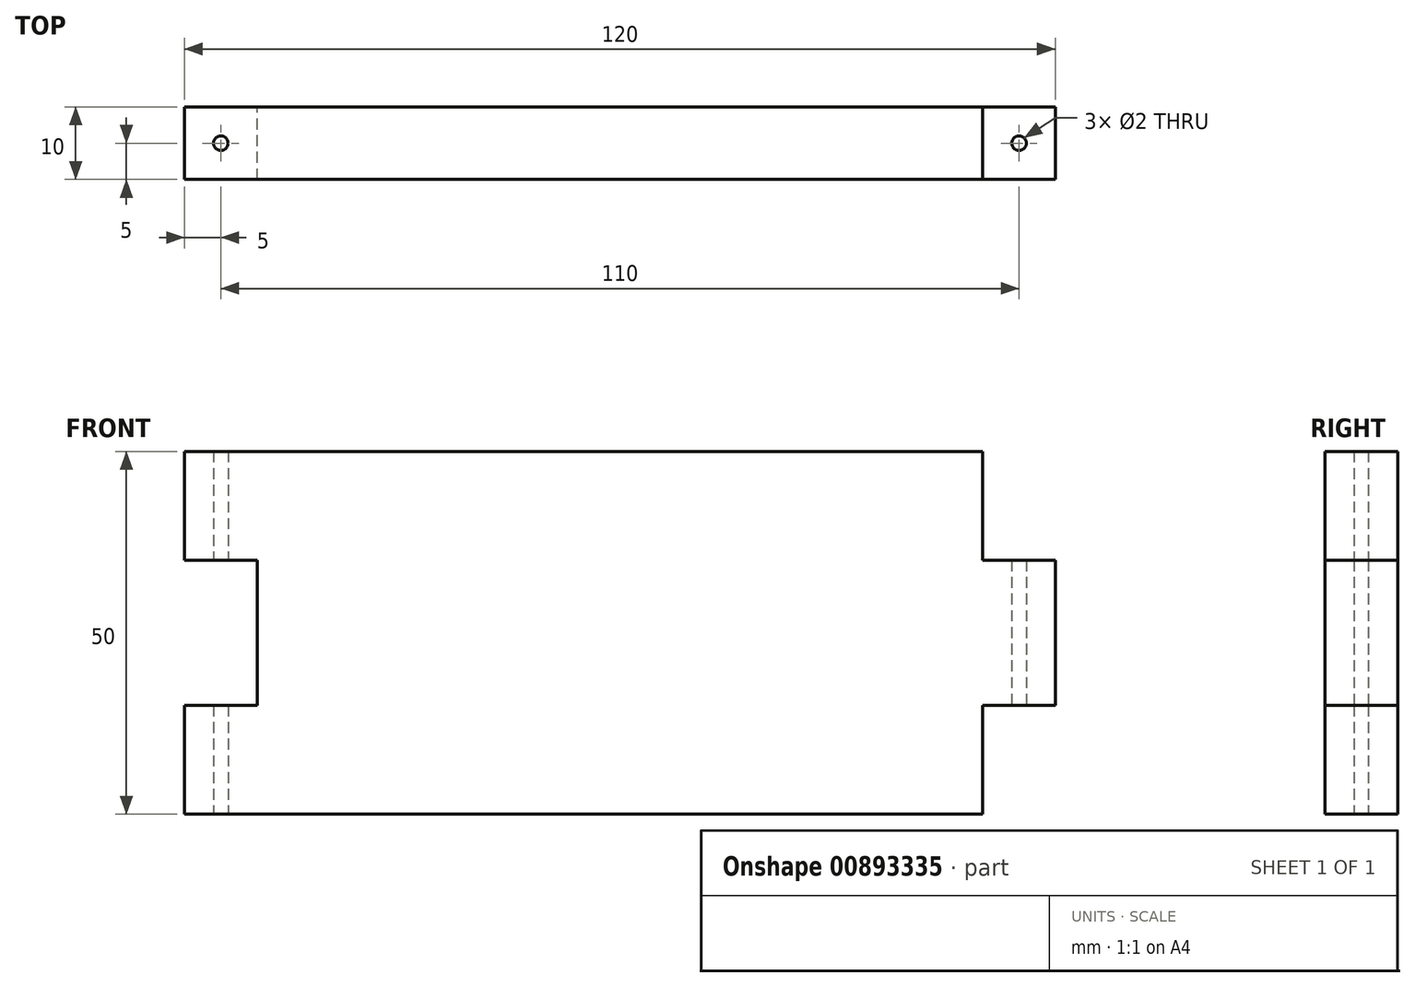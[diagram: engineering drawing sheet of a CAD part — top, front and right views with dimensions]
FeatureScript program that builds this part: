
annotation { "Feature Type Name" : "Feature", "Feature Type Description" : "" }
export const myFeature = defineFeature(function(context is Context, id is Id, definition is map)
    precondition{}
    {
        {
            var Q0;
            Q0=qCreatedBy(makeId("Front.planeOp"),FACE);
            var sketch = newSketch(context, id + "F0", { "sketchPlane" : qUnion([Q0])});
            skLineSegment(sketch, "E0.bottom", {"start": v(-60, -25) * mm, "end": v(50, -25) * mm});
            skLineSegment(sketch, "E0.top", {"start": v(-60, 25) * mm, "end": v(50, 25) * mm});
            skLineSegment(sketch, "E0.left", {"start": v(-60, -25) * mm, "end": v(-60, -10) * mm});
            skLineSegment(sketch, "E0.right", {"start": v(60, -10) * mm, "end": v(60, 10) * mm});
            skPoint(sketch, "E0.middle", {"position": v(0, 0) * mm});
            skLineSegment(sketch, "E1.bottom", {"start": v(60, -10) * mm, "end": v(60, -10) * mm});
            skLineSegment(sketch, "E1.top", {"start": v(60, 10) * mm, "end": v(60, 10) * mm});
            skPoint(sketch, "E1.middle", {"position": v(60, 0) * mm});
            skLineSegment(sketch, "E2", {"start": v(60, 10) * mm, "end": v(50, 10) * mm});
            skLineSegment(sketch, "E3", {"start": v(50, 10) * mm, "end": v(50, 25) * mm});
            skLineSegment(sketch, "E4", {"start": v(60, -10) * mm, "end": v(50, -10) * mm});
            skLineSegment(sketch, "E5", {"start": v(50, -10) * mm, "end": v(50, -25) * mm});
            skPoint(sketch, "E6.orphan", {"position": v(60, 25) * mm});
            skPoint(sketch, "E7.orphan", {"position": v(60, -25) * mm});
            skLineSegment(sketch, "E8", {"start": v(-60, 10) * mm, "end": v(-50, 10) * mm});
            skLineSegment(sketch, "E9", {"start": v(-60, -10) * mm, "end": v(-50, -10) * mm});
            skLineSegment(sketch, "E10", {"start": v(-50, -10) * mm, "end": v(-50, 10) * mm});
            skLineSegment(sketch, "E11.trimOffspring", {"start": v(-60, 10) * mm, "end": v(-60, 25) * mm});
            skSolve(sketch);
        }
        {
            var Q0;
            Q0=makeQuery(id+"F0.imprint","IMPRINT",FACE,{"disambiguationData":[TD([[makeQuery(id+"F0.imprint","IMPRINT",EDGE,{"derivedFrom":sQuery(id+"F0.wireOp",EDGE,"E0.bottom")}),1.0]])]});
            extrude(context, id + "F1", {"entities" : qUnion([Q0]), "depth" : 10 * mm, "offsetDistance" : 25 * mm});
        }
        {
            var Q0;
            Q0=makeQuery(id+"F1.opExtrude","SWEPT_FACE",FACE,{"disambiguationData":[OSD([sQuery(id+"F0.wireOp",EDGE,"E0.bottom")])]});
            var sketch = newSketch(context, id + "F2", { "sketchPlane" : qUnion([Q0])});
            skCircle(sketch, "E12", {"center": v(-55, 5) * mm, "radius": 1 * mm});
            skPoint(sketch, "E13.orphan", {"position": v(-60, 5) * mm});
            skSolve(sketch);
        }
        {
            var Q0;
            Q0 = qSketchRegion(id + "F2", true);
            extrude(context, id + "F3", {"entities" : qUnion([Q0]), "operationType" : NewBodyOperationType.REMOVE, "oppositeDirection" : true, "depth" : 52.9 * mm, "offsetDistance" : 25 * mm});
        }
        {
            var Q0;
            Q0=makeQuery(id+"F1.opExtrude","SWEPT_FACE",FACE,{"disambiguationData":[OSD([sQuery(id+"F0.wireOp",EDGE,"E4")])]});
            var sketch = newSketch(context, id + "F4", { "sketchPlane" : qUnion([Q0])});
            skCircle(sketch, "E14", {"center": v(55, 5) * mm, "radius": 1 * mm});
            skPoint(sketch, "E15.orphan", {"position": v(60, 5) * mm});
            skSolve(sketch);
        }
        {
            var Q0;
            Q0 = qSketchRegion(id + "F4", true);
            extrude(context, id + "F5", {"entities" : qUnion([Q0]), "operationType" : NewBodyOperationType.REMOVE, "oppositeDirection" : true, "depth" : 41.9 * mm, "offsetDistance" : 25 * mm});
        }
    });
